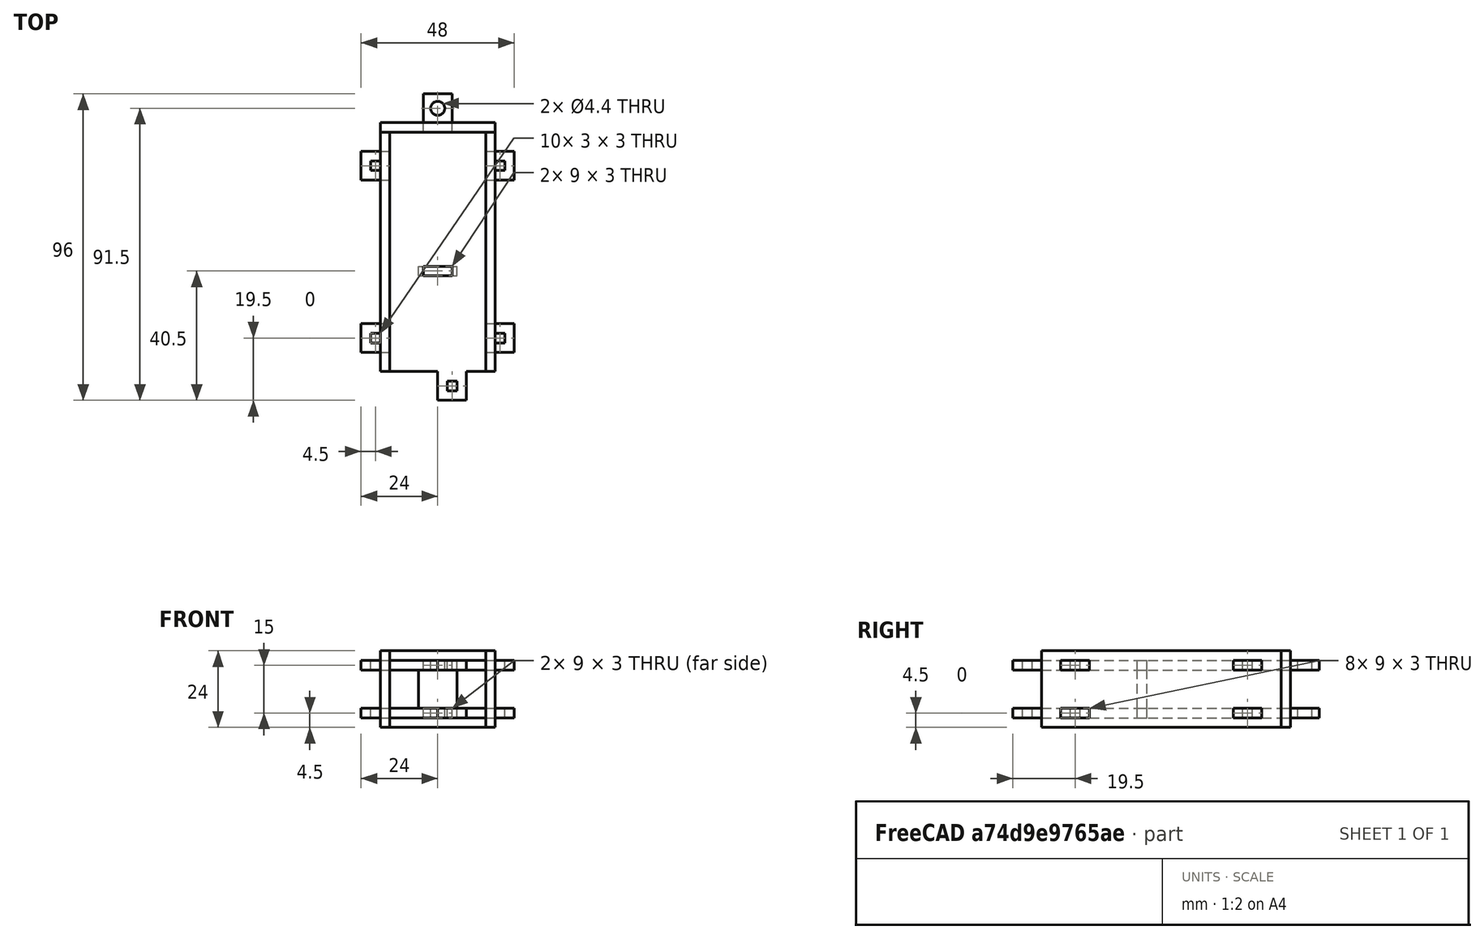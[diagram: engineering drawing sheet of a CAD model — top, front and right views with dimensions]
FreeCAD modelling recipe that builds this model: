
FCSTD DOCUMENT  (FreeCAD 0.16R6707 (Git))
Label: turretPitchHolder
License: All rights reserved
LicenseURL: http://en.wikipedia.org/wiki/All_rights_reserved
objects: Part::Box×44, Part::Cut×26, Part::MultiFuse×7, Part::Cylinder×2
note: 79 computed .brp shape members not serialized (recipe doc carries the construction recipe); baked Part::Feature solids carry a one-line shape summary decoded from their .brp

FEATURE [Part::Box] Box082  label="Cube006"
  Height = 3
  Length = 30
  Width = 75
FEATURE [Part::Box] Box001  label="Cube007"
  Height = 3
  Length = 9
  Placement = pos=(-9,6,0) rot=(0,0,1;0rad)
  Width = 9
FEATURE [Part::Box] Box002  label="Cube008"
  Height = 4
  Length = 3
  Placement = pos=(-6,9,0) rot=(0,0,1;0rad)
  Width = 3
FEATURE [Part::Cut] Cut034
  Base = -> Box001
  Tool = -> Box002
FEATURE [Part::Box] Box003  label="Cube009"
  Height = 3
  Length = 9
  Placement = pos=(-9,6,0) rot=(0,0,1;0rad)
  Width = 9
FEATURE [Part::Box] Box004  label="Cube010"
  Height = 4
  Length = 3
  Placement = pos=(-6,9,0) rot=(0,0,1;0rad)
  Width = 3
FEATURE [Part::Cut] Cut001
  Base = -> Box003
  Placement = pos=(39,0,0) rot=(0,0,1;0rad)
  Tool = -> Box004
FEATURE [Part::Box] Box005  label="Cube011"
  Height = 3
  Length = 9
  Placement = pos=(10.5,30,0) rot=(0,0,1;0rad)
  Width = 3
FEATURE [Part::Cut] Cut002
  Base = -> Box082
  Tool = -> Box005
FEATURE [Part::MultiFuse] Fusion027
  Shapes = -> [Cut034,Cut001,Cut002]
FEATURE [Part::Box] Box006  label="Cube012"
  Height = 3
  Length = 9
  Placement = pos=(10.5,36,0) rot=(0,0,1;0rad)
  Width = 9
FEATURE [Part::Cylinder] Cylinder027  label="RotationHoie"
  Angle = 360
  Height = 10
  Placement = pos=(15,40.5,0) rot=(0,0,1;0rad)
  Radius = 2.2
FEATURE [Part::Cut] Cut003
  Base = -> Box006
  Placement = pos=(0,42,0) rot=(0,0,1;0rad)
  Tool = -> Cylinder027
FEATURE [Part::Box] Box083  label="Cube013"
  Height = 3
  Length = 9
  Placement = pos=(-9,6,0) rot=(0,0,1;0rad)
  Width = 9
FEATURE [Part::Box] Box084  label="Cube014"
  Height = 4
  Length = 3
  Placement = pos=(-6,9,0) rot=(0,0,1;0rad)
  Width = 3
FEATURE [Part::Cut] Cut035
  Base = -> Box083
  Placement = pos=(24,-15,0) rot=(0,0,1;0rad)
  Tool = -> Box084
FEATURE [Part::Box] Box085  label="Cube015"
  Height = 3
  Length = 9
  Placement = pos=(-9,6,0) rot=(0,0,1;0rad)
  Width = 9
FEATURE [Part::Box] Box086  label="Cube016"
  Height = 4
  Length = 3
  Placement = pos=(-6,9,0) rot=(0,0,1;0rad)
  Width = 3
FEATURE [Part::Cut] Cut036
  Base = -> Box085
  Placement = pos=(39,54,0) rot=(0,0,1;0rad)
  Tool = -> Box086
FEATURE [Part::Box] Box087  label="Cube017"
  Height = 3
  Length = 9
  Placement = pos=(-9,6,0) rot=(0,0,1;0rad)
  Width = 9
FEATURE [Part::Box] Box088  label="Cube018"
  Height = 4
  Length = 3
  Placement = pos=(-6,9,0) rot=(0,0,1;0rad)
  Width = 3
FEATURE [Part::Cut] Cut037
  Base = -> Box087
  Placement = pos=(0,54,0) rot=(0,0,1;0rad)
  Tool = -> Box088
FEATURE [Part::MultiFuse] Fusion  label="Fusion001"
  Shapes = -> [Cut003,Cut035,Cut036,Cut037,Fusion027]
FEATURE [Part::Box] Box111  label="Cube033"
  Height = 3
  Length = 9
  Placement = pos=(1,12,15) rot=(0,0,1;0rad)
  Width = 3
FEATURE [Part::Box] Box112  label="Cube034"
  Height = 3
  Length = 9
  Placement = pos=(1,12,0) rot=(0,0,1;0rad)
  Width = 3
FEATURE [Part::Box] Box  label="Cube"
  Height = 12
  Length = 12
  Placement = pos=(-0.5,12,3) rot=(0,0,1;0rad)
  Width = 3
FEATURE [Part::MultiFuse] Fusion030  label="turretPitchHolderDistant"
  Placement = pos=(9.5,18,0) rot=(0,0,1;0rad)
  Shapes = -> [Box112,Box,Box111]
FEATURE [Part::Box] Box113  label="Cube035"
  Height = 3
  Length = 3
  Placement = pos=(30,60,0) rot=(0,0,1;0rad)
  Width = 9
FEATURE [Part::Box] Box114  label="Cube036"
  Height = 3
  Length = 3
  Placement = pos=(39,6,0) rot=(0,0,1;0rad)
  Width = 9
FEATURE [Part::Box] Box115  label="Cube037"
  Height = 3
  Length = 3
  Placement = pos=(39,6,15) rot=(0,0,1;0rad)
  Width = 9
FEATURE [Part::Box] Box116  label="Cube038"
  Height = 3
  Length = 3
  Placement = pos=(39,60,15) rot=(0,0,1;0rad)
  Width = 9
FEATURE [Part::Box] Box117  label="Cube039"
  Height = 24
  Length = 3
  Placement = pos=(39,0,-3) rot=(0,0,1;0rad)
  Width = 75
FEATURE [Part::Cut] Cut
  Base = -> Box117
  Tool = -> Box116
FEATURE [Part::Cut] Cut045
  Base = -> Cut
  Tool = -> Box115
FEATURE [Part::Cut] Cut046
  Base = -> Cut045
  Tool = -> Box114
FEATURE [Part::Cut] Cut047  label="Cutx058"
  Base = -> Cut046
  Placement = pos=(-9,0,0) rot=(0,0,1;0rad)
  Tool = -> Box113
FEATURE [Part::Box] Box123  label="Cube045"
  Height = 3
  Length = 9
  Placement = pos=(10.5,-3,0) rot=(0,0,1;0rad)
  Width = 3
FEATURE [Part::Box] Box124  label="Cube046"
  Height = 24
  Length = 36
  Placement = pos=(-3,-3,-3) rot=(0,0,1;0rad)
  Width = 3
FEATURE [Part::Cut] Cut052
  Base = -> Box124
  Tool = -> Box123
FEATURE [Part::Box] Box125  label="Cube047"
  Height = 3
  Length = 9
  Placement = pos=(10.5,-3,15) rot=(0,0,1;0rad)
  Width = 3
FEATURE [Part::Cut] Cut058  label="turretPitchHolderTopPlate"
  Base = -> Cut052
  Placement = pos=(0,78,0) rot=(0,0,1;0rad)
  Tool = -> Box125
FEATURE [Part::Box] Box126  label="Cube048"
  Height = 3
  Length = 9
  Placement = pos=(10.5,75,0) rot=(0,0,1;0rad)
  Width = 3
FEATURE [Part::MultiFuse] Fusion031  label="turretPitchHolderSide"
  Shapes = -> [Fusion,Box126]
FEATURE [Part::Cut] Cut059  label="turretPitchHolderSidePlate"
  Base = -> Cut047
  Tool = -> Box113
FEATURE [Part::Box] Box127  label="Cube049"
  Height = 3
  Length = 3
  Placement = pos=(30,60,0) rot=(0,0,1;0rad)
  Width = 9
FEATURE [Part::Box] Box128  label="Cube050"
  Height = 3
  Length = 3
  Placement = pos=(39,6,0) rot=(0,0,1;0rad)
  Width = 9
FEATURE [Part::Box] Box129  label="Cube051"
  Height = 3
  Length = 3
  Placement = pos=(39,6,15) rot=(0,0,1;0rad)
  Width = 9
FEATURE [Part::Box] Box130  label="Cube052"
  Height = 3
  Length = 3
  Placement = pos=(39,60,15) rot=(0,0,1;0rad)
  Width = 9
FEATURE [Part::Box] Box131  label="Cube053"
  Height = 24
  Length = 3
  Placement = pos=(39,0,-3) rot=(0,0,1;0rad)
  Width = 75
FEATURE [Part::Cut] Cut060
  Base = -> Box131
  Tool = -> Box130
FEATURE [Part::Cut] Cut061
  Base = -> Cut060
  Tool = -> Box129
FEATURE [Part::Cut] Cut062
  Base = -> Cut061
  Tool = -> Box128
FEATURE [Part::Cut] Cut063  label="Cutx059"
  Base = -> Cut062
  Placement = pos=(-9,0,0) rot=(0,0,1;0rad)
  Tool = -> Box127
FEATURE [Part::Cut] Cut064  label="turretPitchHolderSidePlate001"
  Base = -> Cut063
  Placement = pos=(-33,0,0) rot=(0,0,1;0rad)
  Tool = -> Box127
FEATURE [Part::Box] Box132  label="Cube054"
  Height = 3
  Length = 30
  Width = 75
FEATURE [Part::Box] Box133  label="Cube055"
  Height = 3
  Length = 9
  Placement = pos=(-9,6,0) rot=(0,0,1;0rad)
  Width = 9
FEATURE [Part::Box] Box134  label="Cube056"
  Height = 4
  Length = 3
  Placement = pos=(-6,9,0) rot=(0,0,1;0rad)
  Width = 3
FEATURE [Part::Cut] Cut065
  Base = -> Box133
  Tool = -> Box134
FEATURE [Part::Box] Box135  label="Cube057"
  Height = 3
  Length = 9
  Placement = pos=(-9,6,0) rot=(0,0,1;0rad)
  Width = 9
FEATURE [Part::Box] Box136  label="Cube058"
  Height = 4
  Length = 3
  Placement = pos=(-6,9,0) rot=(0,0,1;0rad)
  Width = 3
FEATURE [Part::Cut] Cut066
  Base = -> Box135
  Placement = pos=(39,0,0) rot=(0,0,1;0rad)
  Tool = -> Box136
FEATURE [Part::Box] Box137  label="Cube059"
  Height = 3
  Length = 9
  Placement = pos=(10.5,30,0) rot=(0,0,1;0rad)
  Width = 3
FEATURE [Part::Cut] Cut067
  Base = -> Box132
  Tool = -> Box137
FEATURE [Part::MultiFuse] Fusion032
  Shapes = -> [Cut065,Cut066,Cut067]
FEATURE [Part::Box] Box138  label="Cube060"
  Height = 3
  Length = 9
  Placement = pos=(10.5,36,0) rot=(0,0,1;0rad)
  Width = 9
FEATURE [Part::Cylinder] Cylinder028  label="RotationHoie001"
  Angle = 360
  Height = 10
  Placement = pos=(15,40.5,0) rot=(0,0,1;0rad)
  Radius = 2.2
FEATURE [Part::Cut] Cut068
  Base = -> Box138
  Placement = pos=(0,42,0) rot=(0,0,1;0rad)
  Tool = -> Cylinder028
FEATURE [Part::Box] Box139  label="Cube061"
  Height = 3
  Length = 9
  Placement = pos=(-9,6,0) rot=(0,0,1;0rad)
  Width = 9
FEATURE [Part::Box] Box140  label="Cube062"
  Height = 4
  Length = 3
  Placement = pos=(-6,9,0) rot=(0,0,1;0rad)
  Width = 3
FEATURE [Part::Cut] Cut069
  Base = -> Box139
  Placement = pos=(24,-15,0) rot=(0,0,1;0rad)
  Tool = -> Box140
FEATURE [Part::Box] Box141  label="Cube063"
  Height = 3
  Length = 9
  Placement = pos=(-9,6,0) rot=(0,0,1;0rad)
  Width = 9
FEATURE [Part::Box] Box142  label="Cube064"
  Height = 4
  Length = 3
  Placement = pos=(-6,9,0) rot=(0,0,1;0rad)
  Width = 3
FEATURE [Part::Cut] Cut070
  Base = -> Box141
  Placement = pos=(39,54,0) rot=(0,0,1;0rad)
  Tool = -> Box142
FEATURE [Part::Box] Box143  label="Cube065"
  Height = 3
  Length = 9
  Placement = pos=(-9,6,0) rot=(0,0,1;0rad)
  Width = 9
FEATURE [Part::Box] Box144  label="Cube066"
  Height = 4
  Length = 3
  Placement = pos=(-6,9,0) rot=(0,0,1;0rad)
  Width = 3
FEATURE [Part::Cut] Cut071
  Base = -> Box143
  Placement = pos=(0,54,0) rot=(0,0,1;0rad)
  Tool = -> Box144
FEATURE [Part::MultiFuse] Fusion033  label="Fusion035"
  Shapes = -> [Cut068,Cut069,Cut070,Cut071,Fusion032]
FEATURE [Part::Box] Box145  label="Cube067"
  Height = 3
  Length = 9
  Placement = pos=(10.5,75,0) rot=(0,0,1;0rad)
  Width = 3
FEATURE [Part::MultiFuse] Fusion034  label="turretPitchHolderSide001"
  Placement = pos=(0,0,15) rot=(0,0,1;0rad)
  Shapes = -> [Fusion033,Box145]
